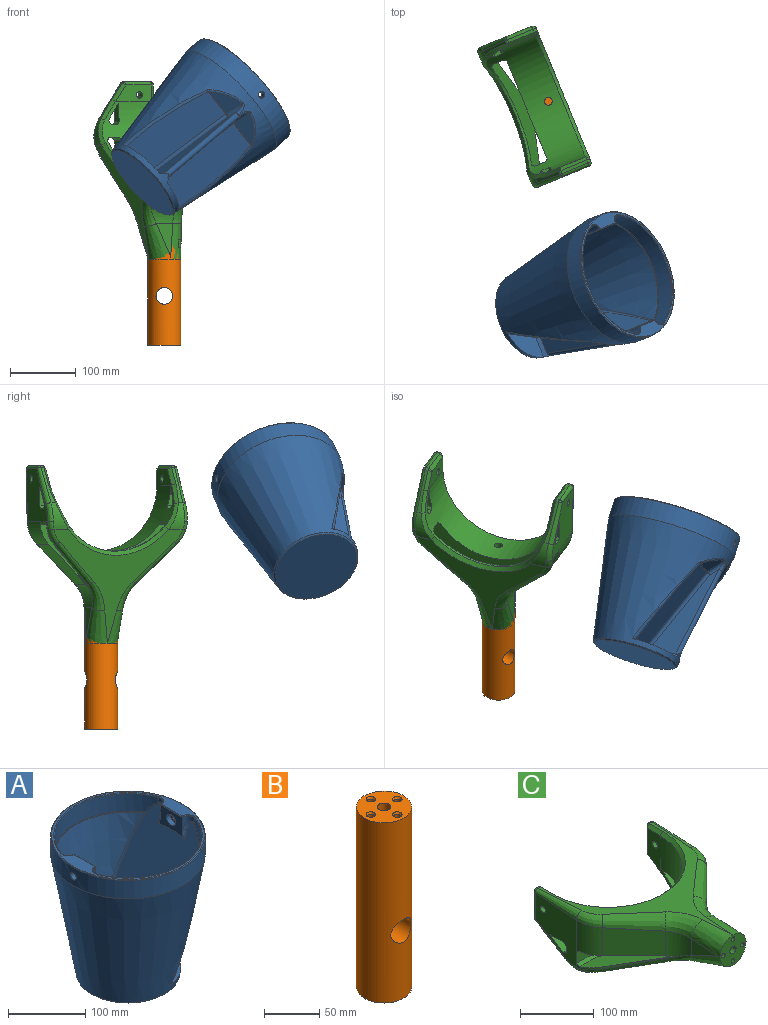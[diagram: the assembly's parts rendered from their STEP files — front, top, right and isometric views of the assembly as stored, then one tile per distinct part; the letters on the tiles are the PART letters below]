
ASSEMBLY  parts=3 mates=2
PART A: 90 faces, bbox 218.3x218.3x269.7 mm
  f0: cone r=66.5mm half-angle=10deg, axis (0,0,1), area 75028.9mm2, adj f4,f49,f65,f69,f71,f72,f73,f76
  f1: cylinder r=95mm len=177.77mm, axis (0,0,1), area 6168.4mm2, adj f13,f25,f30,f37,f50
  f2: cylinder r=5.25mm len=14mm, axis (1,0,0), area 461.8mm2, adj f4,f11
  f3: cylinder r=95mm len=177.77mm, axis (0,0,1), area 6168.4mm2, adj f14,f18,f26,f46,f61
  f4: cylinder r=100mm len=200mm, axis (0,0,1), area 18048mm2, adj f0,f2,f6,f62
  f5: plane 198x198mm, normal (0,0,1), area 3211.5mm2, adj f50,f51,f54,f55,f58,f59,f60,f61
  f6: cylinder r=5.25mm len=14mm, axis (1,0,0), area 461.8mm2, adj f4,f23
  f7: plane 24.22x0.92mm, normal (0,0,-1), area 14.9mm2, adj f10,f15
  f8: plane 20.09x0.53mm, normal (0,-1,0), area 10.3mm2, adj f10,f14,f48,f57
  f9: plane 20.09x0.53mm, normal (0,1,0), area 10.3mm2, adj f10,f13,f35,f53
  f10: plane 46.55x32.38mm, normal (-1,0,0), area 976.5mm2, adj f7,f8,f9,f12,f15,f35,f48,f58
  f11: plane 16.5x16.5mm, normal (-1,0,0), area 127.2mm2, adj f2,f12
  f12: cylinder r=8.25mm len=16.5mm, axis (-1,0,0), area 362.9mm2, adj f10,f11
  f13: cylinder r=10mm len=18.84mm, axis (0,0,1), area 204.6mm2, adj f1,f9,f36,f54
  f14: cylinder r=10mm len=18.84mm, axis (0,0,1), area 204.6mm2, adj f3,f8,f47,f60
  f15: cone r=79.92mm half-angle=40deg, axis (0,0,-1), area 47.9mm2, adj f7,f10,f17,f35,f48
  f16: plane 129x129mm, normal (0,0,-1), area 13068.9mm2, adj f49
  f17: plane 201.94x128.84mm, normal (-0.92,0,0.39), area 24495.9mm2, adj f15,f35,f36,f37,f38,f39,f42,f44
  f18: torus R=85mm, axis (0,0,-1), area 365.9mm2, adj f3,f29,f33,f45
  f19: plane 24.22x0.92mm, normal (0,0,-1), area 14.9mm2, adj f22,f27
  f20: plane 30.5x0.53mm, normal (0,-1,0), area 15.4mm2, adj f22,f26,f28,f56
  f21: plane 30.5x0.53mm, normal (0,1,0), area 15.4mm2, adj f22,f25,f32,f52
  f22: plane 40.31x31.17mm, normal (1,0,0), area 959.8mm2, adj f19,f20,f21,f24,f27,f28,f32,f55
  f23: plane 16.5x16.5mm, normal (1,0,0), area 127.2mm2, adj f6,f24
  f24: cylinder r=8.25mm len=16.5mm, axis (1,0,0), area 362.9mm2, adj f22,f23
  f25: cylinder r=10mm len=27.69mm, axis (0,0,1), area 534.8mm2, adj f1,f21,f31,f51
  f26: cylinder r=10mm len=27.69mm, axis (0,0,1), area 534.8mm2, adj f3,f20,f29,f59
  f27: cone r=79.92mm half-angle=40deg, axis (0,0,-1), area 871.4mm2, adj f19,f22,f28,f32,f33
  f28: bspline ~110.09x33.77mm, area 195.7mm2, adj f20,f22,f27,f29,f33
  f29: sphere r=10mm, area 25.2mm2, adj f18,f26,f28
  f30: torus R=85mm, axis (0,0,-1), area 365.9mm2, adj f1,f31,f33,f38
  f31: sphere r=10mm, area 25.2mm2, adj f25,f30,f32
  f32: bspline ~110.09x33.77mm, area 195.7mm2, adj f21,f22,f27,f31,f33
  f33: cone r=61.57mm half-angle=10deg, axis (0,0,1), area 59517.5mm2, adj f18,f27,f28,f30,f32,f39,f41,f44
  f34: plane 116.19x56.92mm, normal (0,0,1), area 5165.7mm2, adj f41,f42
  f35: cylinder r=5mm len=13.78mm, axis (0.39,0,0.92), area 68.9mm2, adj f9,f10,f15,f17,f36
  f36: bspline ~13.73x13.53mm, area 89.6mm2, adj f13,f17,f35,f37
  f37: bspline ~21.82x19.49mm, area 84.6mm2, adj f1,f17,f36,f38
  f38: bspline ~3.73x3.29mm, area 4.6mm2, adj f17,f30,f37,f39
  f39: bspline ~212.43x94.82mm, area 1025.5mm2, adj f17,f33,f38,f40
  f40: sphere r=5mm, area 13.9mm2, adj f39,f41,f42
  f41: torus R=58.11mm, axis (0,0,1), area 1321.9mm2, adj f33,f34,f40,f43
  f42: cylinder r=5mm len=116.19mm, axis (0,1,0), area 679.3mm2, adj f17,f34,f40,f43
  f43: sphere r=5mm, area 25.6mm2, adj f41,f42,f44
  f44: bspline ~212.43x94.82mm, area 1025.5mm2, adj f17,f33,f43,f45
  f45: bspline ~3.73x3.29mm, area 4.6mm2, adj f17,f18,f44,f46
  f46: bspline ~21.82x19.49mm, area 84.6mm2, adj f3,f17,f45,f47
  f47: bspline ~13.73x13.53mm, area 89.6mm2, adj f14,f17,f46,f48
  f48: cylinder r=5mm len=13.78mm, axis (0.39,0,0.92), area 68.9mm2, adj f8,f10,f15,f17,f47
  f49: cone r=66.85mm half-angle=50deg, axis (0,0,1), area 1264.4mm2, adj f0,f16
  f50: torus R=96mm, axis (0,0,-1), area 362.5mm2, adj f1,f5,f51,f54
  f51: torus R=11mm, axis (0,0,-1), area 31.3mm2, adj f5,f25,f50,f52,f55
  f52: cylinder r=1mm len=0.88mm, axis (-1,0,0), area 0.3mm2, adj f21,f51,f55
  f53: cylinder r=1mm len=0.88mm, axis (1,0,0), area 0.3mm2, adj f9,f54,f58
  f54: torus R=11mm, axis (0,0,-1), area 31.3mm2, adj f5,f13,f50,f53,f58
  f55: cylinder r=1mm len=40mm, axis (0,1,0), area 61.5mm2, adj f5,f22,f51,f52,f56,f59
  f56: cylinder r=1mm len=0.88mm, axis (1,0,0), area 0.3mm2, adj f20,f55,f59
  f57: cylinder r=1mm len=0.88mm, axis (-1,0,0), area 0.3mm2, adj f8,f58,f60
  f58: cylinder r=1mm len=40mm, axis (0,1,0), area 61.5mm2, adj f5,f10,f53,f54,f57,f60
  f59: torus R=11mm, axis (0,0,-1), area 31.3mm2, adj f5,f26,f55,f56,f61
  f60: torus R=11mm, axis (0,0,-1), area 31.3mm2, adj f5,f14,f57,f58,f61
  f61: torus R=96mm, axis (0,0,-1), area 362.5mm2, adj f3,f5,f59,f60
  f62: torus R=99mm, axis (0,0,-1), area 983.4mm2, adj f4,f5
  f63: plane 42.33x21.9mm, normal (0.73,0,-0.68), area 806mm2, adj f74,f81,f82
  f64: plane 139.19x59.08mm, normal (0.92,0,-0.39), area 7921.5mm2, adj f65,f73,f74,f75
  f65: plane 57.4x56.7mm, normal (0,0,1), area 2111mm2, adj f0,f64,f72,f73
  f66: plane 143.59x66.72mm, normal (0,1,0), area 3354.2mm2, adj f72,f75,f82,f88
  f67: plane 42.33x21.9mm, normal (0.73,0,-0.68), area 806mm2, adj f79,f86,f87
  f68: plane 139.19x59.08mm, normal (0.92,0,-0.39), area 7921.5mm2, adj f69,f78,f79,f80
  f69: plane 57.4x56.7mm, normal (0,0,1), area 2111mm2, adj f0,f68,f71,f80
  f70: plane 143.59x66.72mm, normal (0,-1,0), area 3354.2mm2, adj f71,f78,f86,f88
  f71: plane 56.71x11.79mm, normal (0,-0.71,0.71), area 367.5mm2, adj f0,f69,f70,f78,f88
  f72: plane 56.71x11.79mm, normal (0,0.71,0.71), area 367.5mm2, adj f0,f65,f66,f75,f88
  f73: bspline ~181.41x81.07mm, area 764.3mm2, adj f0,f64,f65,f76
  f74: cylinder r=5mm len=43.98mm, axis (0,-1,0), area 75.3mm2, adj f63,f64,f76,f77
  f75: cylinder r=5mm len=141.14mm, axis (0.39,0,0.92), area 1157.9mm2, adj f64,f66,f72,f77
  f76: bspline ~5.95x5.42mm, area 11.3mm2, adj f0,f73,f74,f81
  f77: sphere r=5mm, area 11mm2, adj f74,f75,f82
  f78: cylinder r=5mm len=141.14mm, axis (0.39,0,0.92), area 1157.9mm2, adj f68,f70,f71,f83
  f79: cylinder r=5mm len=43.98mm, axis (0,1,0), area 75.3mm2, adj f67,f68,f83,f84
  f80: bspline ~181.41x81.07mm, area 764.3mm2, adj f0,f68,f69,f84
  f81: bspline ~50x27.81mm, area 182.8mm2, adj f0,f63,f76,f85
  f82: cylinder r=5mm len=25.31mm, axis (0.68,0,0.73), area 178.6mm2, adj f63,f66,f77,f85
  f83: sphere r=5mm, area 11mm2, adj f78,f79,f86
  f84: bspline ~5.45x5.18mm, area 11.3mm2, adj f0,f79,f80,f87
  f85: bspline ~18.27x11.51mm, area 101.3mm2, adj f0,f81,f82,f88
  f86: cylinder r=5mm len=25.31mm, axis (0.68,0,0.73), area 178.6mm2, adj f67,f70,f83,f89
  f87: bspline ~50x27.81mm, area 182.8mm2, adj f0,f67,f84,f89
  f88: cylinder r=5mm len=144.46mm, axis (0.17,0,0.98), area 2243.6mm2, adj f66,f70,f71,f72,f85,f89
  f89: bspline ~18.4x10.9mm, area 101.3mm2, adj f0,f86,f87,f88
PART B: 30 faces, bbox 50x50x200 mm
  f0: cylinder r=25mm len=200mm, axis (0,0,-1), area 30052mm2, adj f1,f2,f8,f24,f27,f28,f29
  f1: plane 50x50mm, normal (0,0,1), area 1617.5mm2, adj f0,f17,f18,f19,f20,f21
  f2: plane 50x50mm, normal (0,0,-1), area 1039mm2, adj f0,f7
  f3: plane 32x32mm, normal (0,0,-1), area 297.5mm2, adj f4,f6
  f4: cylinder r=16mm len=32mm, axis (0,0,-1), area 2312.2mm2, adj f3,f7
  f5: cone r=0mm half-angle=59deg, axis (0,0,-1), area 591.1mm2, adj f6
  f6: cylinder r=12.7mm len=25.4mm, axis (0,0,1), area 987mm2, adj f3,f5
  f7: cone r=16mm half-angle=30deg, axis (0,0,-1), area 240.5mm2, adj f2,f4
  f8: cylinder r=12.7mm len=50mm, axis (0,1,0), area 3718.4mm2, adj f0
  f9: cylinder r=3.15mm len=37mm, axis (0,0,1), area 732.3mm2, adj f10,f17
  f10: plane 6.3x6.3mm, normal (0,0,1), area 31.2mm2, adj f9
  f11: cylinder r=3.15mm len=37mm, axis (0,0,1), area 732.3mm2, adj f12,f19
  f12: plane 6.3x6.3mm, normal (0,0,1), area 31.2mm2, adj f11
  f13: cylinder r=3.15mm len=37mm, axis (0,0,1), area 732.3mm2, adj f14,f20
  f14: plane 6.3x6.3mm, normal (0,0,1), area 31.2mm2, adj f13
  f15: cylinder r=3.15mm len=37mm, axis (0,0,1), area 732.3mm2, adj f16,f18
  f16: plane 6.3x6.3mm, normal (0,0,1), area 31.2mm2, adj f15
  f17: cone r=3.15mm half-angle=30deg, axis (0,0,1), area 54.1mm2, adj f1,f9
  f18: cone r=3.15mm half-angle=30deg, axis (0,0,1), area 54.1mm2, adj f1,f15
  f19: cone r=3.15mm half-angle=30deg, axis (0,0,1), area 54.1mm2, adj f1,f11
  f20: cone r=3.15mm half-angle=30deg, axis (0,0,1), area 54.1mm2, adj f1,f13
  f21: cylinder r=6mm len=40mm, axis (0,0,1), area 1508mm2, adj f1,f24
  f22: plane 25.4x12mm, normal (0,1,0), area 304.8mm2, adj f24,f25,f27,f28
  f23: plane 25.4x12mm, normal (0,-1,0), area 304.8mm2, adj f24,f26,f27,f29
  f24: plane 35.97x25mm, normal (0,0,-1), area 511.5mm2, adj f0,f21,f22,f23,f25,f26,f28,f29
  f25: plane 12x9.5mm, normal (0.87,0.5,0), area 131.6mm2, adj f22,f24,f26,f27
  f26: plane 12x9.5mm, normal (0.87,-0.5,0), area 131.6mm2, adj f23,f24,f25,f27
  f27: plane 35.97x25mm, normal (0,0,1), area 624.6mm2, adj f0,f22,f23,f25,f26,f28,f29
  f28: cylinder r=2mm len=12mm, axis (0,0,-1), area 50.3mm2, adj f0,f22,f24,f27
  f29: cylinder r=2mm len=12mm, axis (0,0,-1), area 50.3mm2, adj f0,f23,f24,f27
PART C: 103 faces, bbox 234.2x285.8x100 mm
  f0: plane 60.71x60.71mm, normal (0.71,-0.71,0), area 3780mm2, adj f5,f29,f30,f36
  f1: plane 61.1x61.1mm, normal (-0.71,-0.71,0), area 224.4mm2, adj f6,f28,f31,f53
  f2: plane 270.56x220.23mm, normal (0,0,1), area 7443mm2, adj f34,f35,f36,f37,f38,f39,f40,f41
  f3: plane 53.2x53.2mm, normal (0,-1,0), area 1680.3mm2, adj f34,f43,f50,f51,f94,f95,f97,f99
  f4: plane 213.63x174.62mm, normal (0,-0.25,-0.97), area 9366.1mm2, adj f32,f33,f47,f48,f49,f50,f51,f52
  f5: plane 229.58x101.86mm, normal (0,0,-1), area 11334mm2, adj f0,f6,f21,f27,f28,f29,f30,f31
  f6: plane 230.01x101.53mm, normal (0,0.25,0.97), area 11632.5mm2, adj f1,f5,f21,f24,f28,f29,f30,f31
  f7: plane 54.37x36.3mm, normal (0,0.55,-0.83), area 322.8mm2, adj f32,f57,f77,f88,f90
  f8: plane 42.32x5mm, normal (0,1,0), area 211.6mm2, adj f68,f69,f70,f71,f72,f83
  f9: plane 31.48x18.23mm, normal (0,-1,0), area 573.9mm2, adj f21,f29,f64,f65
  f10: plane 28.09x19.97mm, normal (0,0,-1), area 472.3mm2, adj f12,f14,f21,f59
  f11: plane 21.33x10.19mm, normal (0,1,0), area 217.2mm2, adj f13,f21,f62,f63
  f12: plane 26.13x19.48mm, normal (0,-0.55,0.83), area 516.9mm2, adj f10,f14,f21,f58
  f13: plane 84.36x84mm, normal (1,0,0), area 4648.2mm2, adj f11,f18,f20,f29,f38,f44,f45,f62
  f14: plane 83.74x79.44mm, normal (-1,0,0), area 4648.2mm2, adj f10,f12,f19,f28,f39,f56,f57,f58
  f15: plane 54.26x36.19mm, normal (0,0.55,-0.83), area 322.8mm2, adj f33,f44,f72,f87,f89
  f16: plane 42.32x5mm, normal (0,1,0), area 211.6mm2, adj f73,f74,f75,f76,f77,f84
  f17: plane 31.48x18.23mm, normal (0,-1,0), area 573.9mm2, adj f21,f28,f60,f61
  f18: plane 28.09x19.97mm, normal (0,0,-1), area 472.3mm2, adj f13,f20,f21,f63
  f19: plane 21.33x10.19mm, normal (0,1,0), area 217.2mm2, adj f14,f21,f58,f59
  f20: plane 26.13x19.48mm, normal (0,-0.55,0.83), area 516.9mm2, adj f13,f18,f21,f62
  f21: cylinder r=100mm len=200mm, axis (0,0,1), area 19891.3mm2, adj f5,f6,f9,f10,f11,f12,f17,f18
  f22: plane 58.99x25mm, normal (1,0,0), area 1187.9mm2, adj f21,f67,f80,f84,f88
  f23: plane 58.99x25mm, normal (-1,0,0), area 1187.9mm2, adj f21,f66,f79,f83,f87
  f24: plane 61.12x61.12mm, normal (0.71,-0.71,0), area 224.4mm2, adj f6,f29,f30,f48
  f25: plane 55.62x28.18mm, normal (1,0,0), area 668.1mm2, adj f30,f34,f50
  f26: plane 55.63x28.2mm, normal (-1,0,0), area 662.3mm2, adj f31,f43,f51
  f27: plane 60.71x60.71mm, normal (-0.71,-0.71,0), area 3780mm2, adj f5,f28,f31,f41
  f28: cylinder r=50mm len=78.29mm, axis (0,0,1), area 2042.7mm2, adj f1,f5,f6,f14,f17,f27,f40,f54
  f29: cylinder r=50mm len=78.29mm, axis (0,0,1), area 2042.7mm2, adj f0,f5,f6,f9,f13,f24,f37,f46
  f30: cylinder r=50mm len=45.63mm, axis (0,0,-1), area 1446.7mm2, adj f0,f5,f6,f24,f25,f35,f49
  f31: cylinder r=50mm len=45.63mm, axis (0,0,-1), area 1446.6mm2, adj f1,f5,f6,f26,f27,f42,f52
  f32: cylinder r=50mm len=40.15mm, axis (-1,0,0), area 684mm2, adj f4,f7,f55,f56,f92
  f33: cylinder r=50mm len=40.15mm, axis (-1,0,0), area 684.1mm2, adj f4,f15,f45,f46,f91
  f34: bspline ~56.99x25.18mm, area 1978.1mm2, adj f2,f3,f25,f35,f50
  f35: bspline ~48.66x36.08mm, area 1423.1mm2, adj f2,f30,f34,f36
  f36: bspline ~74.02x70.01mm, area 2156.6mm2, adj f0,f2,f35,f37
  f37: bspline ~35.36x23.94mm, area 668.6mm2, adj f2,f29,f36,f38
  f38: bspline ~88.51x10.57mm, area 990.2mm2, adj f2,f13,f37,f69
  f39: bspline ~79.29x10.57mm, area 990mm2, adj f2,f14,f40,f74
  f40: bspline ~35.36x23.94mm, area 668.4mm2, adj f2,f28,f39,f41
  f41: bspline ~74.01x70.01mm, area 2156.6mm2, adj f2,f27,f40,f42
  f42: bspline ~48.66x36.07mm, area 1423.1mm2, adj f2,f31,f41,f43
  f43: bspline ~57x25.18mm, area 1977.9mm2, adj f2,f3,f26,f42,f51
  f44: bspline ~57.86x40.38mm, area 592.3mm2, adj f13,f15,f45,f71
  f45: bspline ~27.86x13.82mm, area 301.4mm2, adj f13,f33,f44,f46
  f46: bspline ~13.94x8.82mm, area 148mm2, adj f29,f33,f45,f47
  f47: bspline ~23.92x18.83mm, area 291.5mm2, adj f4,f29,f46,f48
  f48: bspline ~67.81x65.48mm, area 1106mm2, adj f4,f24,f47,f49
  f49: bspline ~46.5x29.8mm, area 831mm2, adj f4,f30,f48,f50
  f50: bspline ~60.52x39.74mm, area 1769.6mm2, adj f3,f4,f25,f34,f49
  f51: bspline ~60.52x39.74mm, area 1770.8mm2, adj f3,f4,f26,f43,f52
  f52: bspline ~46.3x29.79mm, area 829.8mm2, adj f4,f31,f51,f53
  f53: bspline ~67.81x65.48mm, area 1106mm2, adj f1,f4,f52,f54
  f54: bspline ~23.92x18.83mm, area 291.5mm2, adj f4,f28,f53,f55
  f55: bspline ~13.94x8.82mm, area 148mm2, adj f28,f32,f54,f56
  f56: bspline ~27.86x13.82mm, area 301.4mm2, adj f14,f32,f55,f57
  f57: bspline ~65.75x45.46mm, area 592.3mm2, adj f7,f14,f56,f76
  f58: plane 21.34x6.05mm, normal (0,0.47,0.88), area 138.7mm2, adj f12,f14,f19,f21
  f59: plane 21.34x3.89mm, normal (0,0.71,-0.71), area 113.2mm2, adj f10,f14,f19,f21
  f60: plane 34.2x3.91mm, normal (0,-0.71,-0.71), area 179.5mm2, adj f5,f17,f21,f28
  f61: plane 34.92x4.88mm, normal (0,-0.61,0.79), area 202.5mm2, adj f6,f17,f21,f28
  f62: plane 21.34x6.05mm, normal (0,0.47,0.88), area 138.7mm2, adj f11,f13,f20,f21
  f63: plane 21.34x3.89mm, normal (0,0.71,-0.71), area 113.2mm2, adj f11,f13,f18,f21
  f64: plane 34.2x3.91mm, normal (0,-0.71,-0.71), area 179.5mm2, adj f5,f9,f21,f29
  f65: plane 34.92x4.88mm, normal (0,-0.61,0.79), area 202.5mm2, adj f6,f9,f21,f29
  f66: cylinder r=5mm len=15mm, axis (1,0,0), area 471.2mm2, adj f13,f23
  f67: cylinder r=5mm len=15mm, axis (1,0,0), area 471.2mm2, adj f14,f22
  f68: cylinder r=5mm len=5mm, axis (-1,0,0), area 36.7mm2, adj f2,f8,f69,f81
  f69: bspline ~5.45x5.45mm, area 44.1mm2, adj f8,f38,f68,f70
  f70: cylinder r=5mm len=41.92mm, axis (0,0,-1), area 329.3mm2, adj f8,f13,f69,f71
  f71: bspline ~5.66x5.23mm, area 25.4mm2, adj f8,f44,f70,f72
  f72: cylinder r=5mm len=4.94mm, axis (-1,0,0), area 24.3mm2, adj f8,f15,f71,f85
  f73: cylinder r=5mm len=5mm, axis (-1,0,0), area 36.7mm2, adj f2,f16,f74,f82
  f74: bspline ~5.45x5.45mm, area 44.1mm2, adj f16,f39,f73,f75
  f75: cylinder r=5mm len=41.92mm, axis (0,0,1), area 329.3mm2, adj f14,f16,f74,f76
  f76: bspline ~5.66x5.2mm, area 25.4mm2, adj f16,f57,f75,f77
  f77: cylinder r=5mm len=4.94mm, axis (-1,0,0), area 24.3mm2, adj f7,f16,f76,f86
  f78: cone r=100mm half-angle=45deg, axis (0,0,1), area 2277mm2, adj f2,f21,f79,f80
  f79: plane 28.83x8.83mm, normal (-0.71,0,0.71), area 176.8mm2, adj f2,f23,f78,f81
  f80: plane 25x5mm, normal (0.71,0,0.71), area 176.8mm2, adj f2,f22,f78,f82
  f81: cone r=5mm half-angle=45deg, axis (1,0,0), area 18.5mm2, adj f68,f79,f83
  f82: cone r=5mm half-angle=45deg, axis (-1,0,0), area 27.8mm2, adj f73,f80,f84
  f83: plane 42.32x5mm, normal (-0.71,0.71,0), area 299.3mm2, adj f8,f23,f81,f85
  f84: plane 42.32x5mm, normal (0.71,0.71,0), area 299.3mm2, adj f16,f22,f82,f86
  f85: cone r=5mm half-angle=45deg, axis (1,0,0), area 17.4mm2, adj f72,f83,f87
  f86: cone r=5mm half-angle=45deg, axis (-1,0,0), area 17.4mm2, adj f77,f84,f88
  f87: plane 27.77x20.83mm, normal (-0.71,0.39,-0.59), area 212.5mm2, adj f15,f23,f85,f89
  f88: plane 27.77x20.83mm, normal (0.71,0.39,-0.59), area 212.5mm2, adj f7,f22,f86,f90
  f89: bspline ~30.6x23.64mm, area 236.7mm2, adj f15,f21,f87,f91
  f90: bspline ~30.6x23.64mm, area 236.7mm2, adj f7,f21,f88,f92
  f91: bspline ~40.15x22.59mm, area 299.6mm2, adj f21,f33,f89,f93
  f92: bspline ~40.15x22.59mm, area 299.6mm2, adj f21,f32,f90,f93
  f93: bspline ~164.36x44mm, area 1448.1mm2, adj f4,f21,f91,f92
  f94: cylinder r=6mm len=140mm, axis (0,-1,0), area 5277.9mm2, adj f3,f21
  f95: cylinder r=3.5mm len=15mm, axis (0,-1,0), area 329.9mm2, adj f3,f96
  f96: plane 7x7mm, normal (0,-1,0), area 38.5mm2, adj f95
  f97: cylinder r=3.5mm len=15mm, axis (0,-1,0), area 329.9mm2, adj f3,f98
  f98: plane 7x7mm, normal (0,-1,0), area 38.5mm2, adj f97
  f99: cylinder r=3.5mm len=15mm, axis (0,-1,0), area 329.9mm2, adj f3,f100
  f100: plane 7x7mm, normal (0,-1,0), area 38.5mm2, adj f99
  f101: cylinder r=3.5mm len=15mm, axis (0,-1,0), area 329.9mm2, adj f3,f102
  f102: plane 7x7mm, normal (0,-1,0), area 38.5mm2, adj f101
PLACE A rot(axis=(-0.53,0.35,-0.77),82deg) t=(-33.85,-327.12,247.31)mm
PLACE B at identity fixed
PLACE C rot(axis=(0.43,0.64,0.64),133.6deg) t=(0,0,130.77)mm
MATE cylindrical B.f0 <-> C.f94  axis (0,0,1) through (0,0,200)mm
MATE cylindrical C.f66 <-> A.f2  axis (-0.38,0.92,0) through (-38,92.5,380.77)mm
